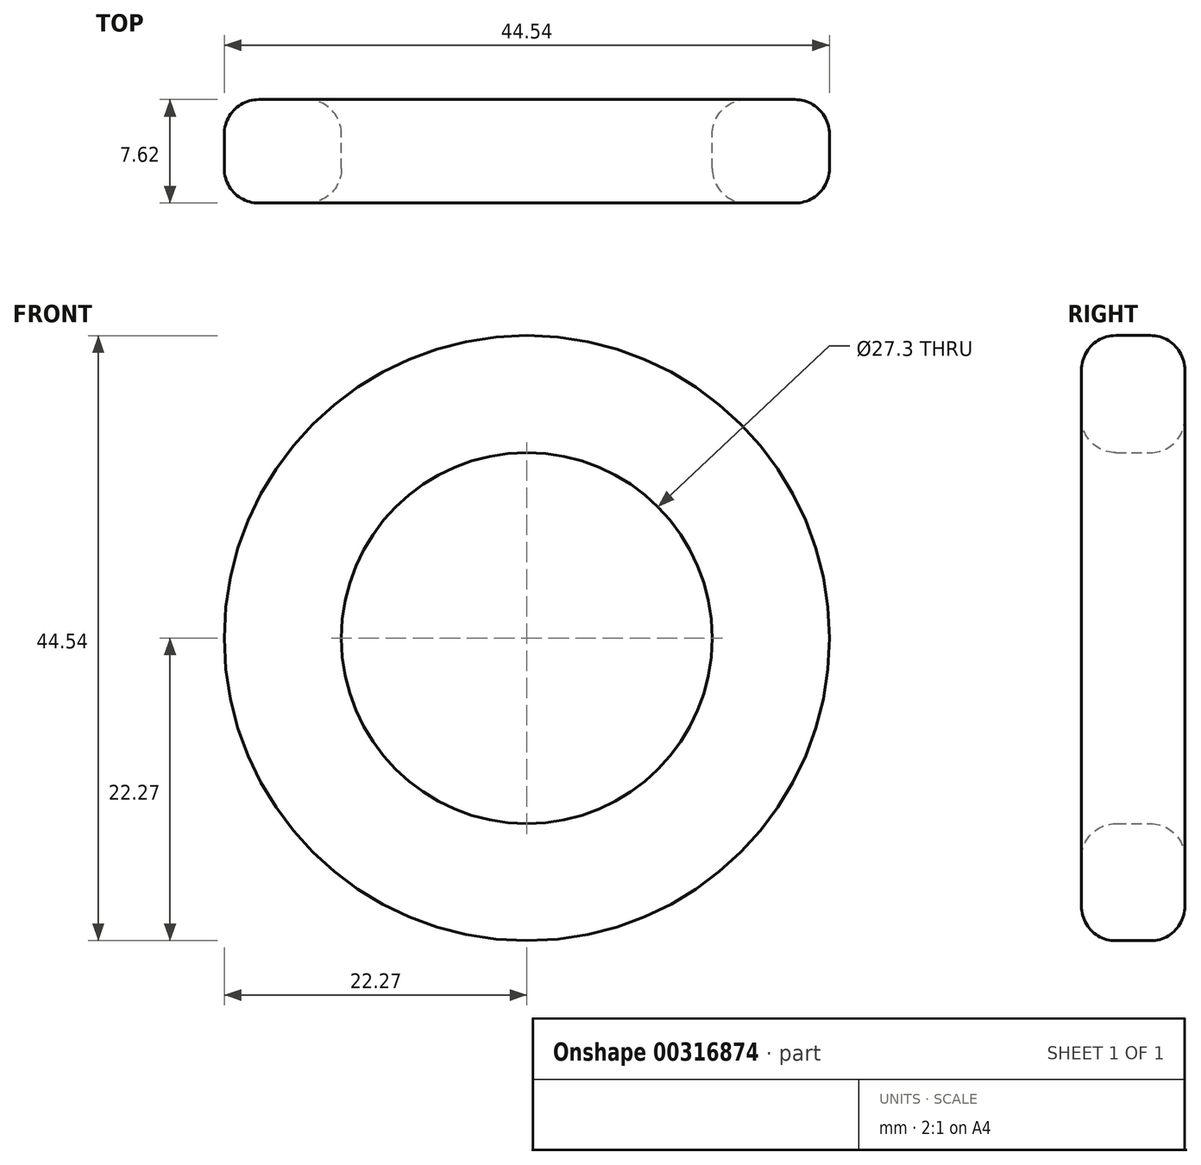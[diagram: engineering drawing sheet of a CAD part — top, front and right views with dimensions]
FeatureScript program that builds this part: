
annotation { "Feature Type Name" : "Feature", "Feature Type Description" : "" }
export const myFeature = defineFeature(function(context is Context, id is Id, definition is map)
    precondition{}
    {
        {
            var Q0;
            Q0=qCreatedBy(makeId("Front.planeOp"),FACE);
            var sketch = newSketch(context, id + "F0", { "sketchPlane" : qUnion([Q0])});
            skCircle(sketch, "E0", {"center": v(0, 0) * mm, "radius": 22.27 * mm});
            skCircle(sketch, "E1", {"center": v(0, 0) * mm, "radius": 13.65 * mm});
            skLineSegment(sketch, "E2", {"start": v(0, -22.27) * mm, "end": v(0, 22.27) * mm});
            skSolve(sketch);
        }
        {
            var Q0;
            {var subQ0=sQuery(id+"F0.wireOp",EDGE,"E2");var subQ1=sQuery(id+"F0.wireOp",EDGE,"E0");var subQ2=makeQuery(id+"F0.imprint","INTERSECT",VERTEX,{"disambiguationData":[OD(0.0)],"derivedFrom":[subQ1,subQ0]});Q0=makeQuery(id+"F0.imprint","IMPRINT",FACE,{"disambiguationData":[TD([[makeQuery(id+"F0.imprint","IMPRINT",EDGE,{"disambiguationData":[TD([[subQ2,-1.0]])],"derivedFrom":subQ1}),1.0]])]});}
            var Q1;
            {var subQ0=sQuery(id+"F0.wireOp",EDGE,"E2");var subQ1=sQuery(id+"F0.wireOp",EDGE,"E0");var subQ2=makeQuery(id+"F0.imprint","INTERSECT",VERTEX,{"disambiguationData":[OD(0.0)],"derivedFrom":[subQ1,subQ0]});Q1=makeQuery(id+"F0.imprint","IMPRINT",FACE,{"disambiguationData":[TD([[makeQuery(id+"F0.imprint","IMPRINT",EDGE,{"disambiguationData":[TD([[subQ2,1.0]])],"derivedFrom":subQ1}),1.0]])]});}
            extrude(context, id + "F1", {"entities" : qUnion([Q0, Q1]), "endBound" : BoundingType.SYMMETRIC, "depth" : 7.62 * mm});
        }
        {
            var Q0;
            Q0=makeQuery(id+"F1.opExtrude","CAP_EDGE",EDGE,{"disambiguationData":[OSD([sQuery(id+"F0.wireOp",EDGE,"E1")])],"isStart":false});
            var Q1;
            Q1=makeQuery(id+"F1.opExtrude","CAP_EDGE",EDGE,{"disambiguationData":[OSD([sQuery(id+"F0.wireOp",EDGE,"E0")])],"isStart":false});
            var Q2;
            Q2=makeQuery(id+"F1.opExtrude","CAP_EDGE",EDGE,{"disambiguationData":[OSD([sQuery(id+"F0.wireOp",EDGE,"E0")])],"isStart":true});
            var Q3;
            Q3=makeQuery(id+"F1.opExtrude","CAP_EDGE",EDGE,{"disambiguationData":[OSD([sQuery(id+"F0.wireOp",EDGE,"E1")])],"isStart":true});
            fillet(context, id + "F2", {"entities" : qUnion([Q0, Q1, Q2, Q3]), "radius" : 2.54 * mm, "tangentPropagation" : true, "allowEdgeOverflow" : false});
        }
    });
